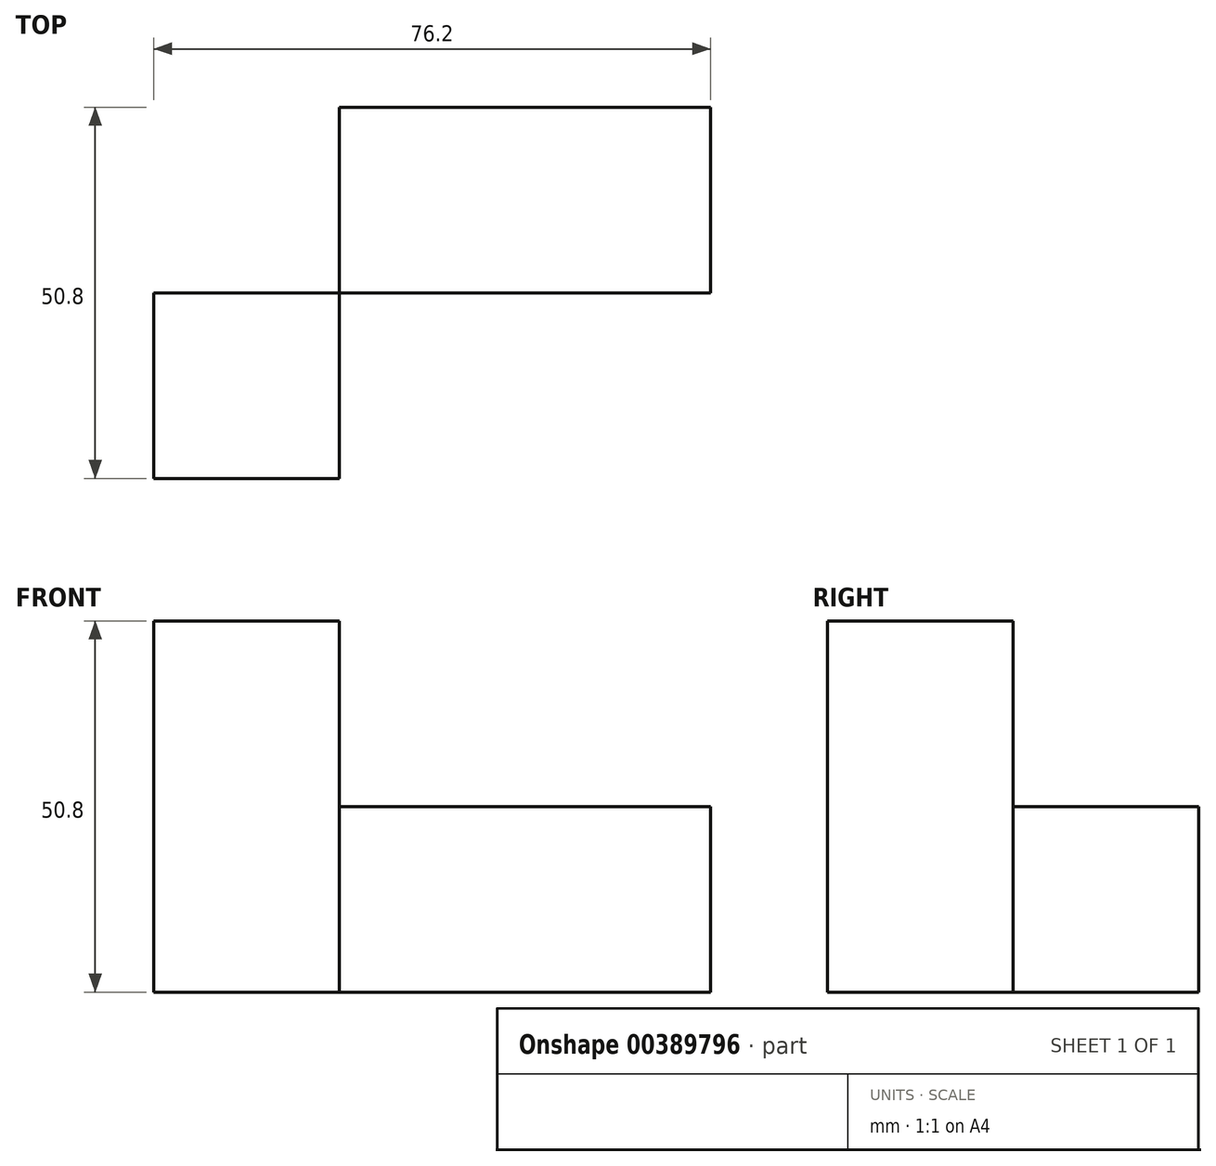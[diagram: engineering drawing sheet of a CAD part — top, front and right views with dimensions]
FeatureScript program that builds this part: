
annotation { "Feature Type Name" : "Feature", "Feature Type Description" : "" }
export const myFeature = defineFeature(function(context is Context, id is Id, definition is map)
    precondition{}
    {
        {
            var Q0;
            Q0=qCreatedBy(makeId("Top.planeOp"),FACE);
            var sketch = newSketch(context, id + "F0", { "sketchPlane" : qUnion([Q0])});
            skLineSegment(sketch, "E0.bottom", {"start": v(0, 0) * mm, "end": v(-25.4, 0) * mm});
            skLineSegment(sketch, "E0.top", {"start": v(0, 25.4) * mm, "end": v(-25.4, 25.4) * mm});
            skLineSegment(sketch, "E0.left", {"start": v(0, 0) * mm, "end": v(0, 25.4) * mm});
            skLineSegment(sketch, "E0.right", {"start": v(-25.4, 0) * mm, "end": v(-25.4, 25.4) * mm});
            skLineSegment(sketch, "E1.bottom", {"start": v(-25.4, 25.4) * mm, "end": v(0, 25.4) * mm});
            skLineSegment(sketch, "E1.top", {"start": v(-25.4, 50.8) * mm, "end": v(0, 50.8) * mm});
            skLineSegment(sketch, "E1.left", {"start": v(-25.4, 25.4) * mm, "end": v(-25.4, 50.8) * mm});
            skLineSegment(sketch, "E1.right", {"start": v(0, 25.4) * mm, "end": v(0, 50.8) * mm});
            skLineSegment(sketch, "E2.bottom", {"start": v(0, 50.8) * mm, "end": v(25.4, 50.8) * mm});
            skLineSegment(sketch, "E2.top", {"start": v(0, 25.4) * mm, "end": v(25.4, 25.4) * mm});
            skLineSegment(sketch, "E2.left", {"start": v(0, 50.8) * mm, "end": v(0, 25.4) * mm});
            skLineSegment(sketch, "E2.right", {"start": v(25.4, 50.8) * mm, "end": v(25.4, 25.4) * mm});
            skLineSegment(sketch, "E3.bottom", {"start": v(25.4, 25.4) * mm, "end": v(50.8, 25.4) * mm});
            skLineSegment(sketch, "E3.top", {"start": v(25.4, 50.8) * mm, "end": v(50.8, 50.8) * mm});
            skLineSegment(sketch, "E3.left", {"start": v(25.4, 25.4) * mm, "end": v(25.4, 50.8) * mm});
            skLineSegment(sketch, "E3.right", {"start": v(50.8, 25.4) * mm, "end": v(50.8, 50.8) * mm});
            skLineSegment(sketch, "E4.bottom", {"start": v(25.4, 25.4) * mm, "end": v(0, 25.4) * mm});
            skLineSegment(sketch, "E4.top", {"start": v(25.4, 0) * mm, "end": v(0, 0) * mm});
            skLineSegment(sketch, "E4.left", {"start": v(25.4, 25.4) * mm, "end": v(25.4, 0) * mm});
            skLineSegment(sketch, "E4.right", {"start": v(0, 25.4) * mm, "end": v(0, 0) * mm});
            skSolve(sketch);
        }
        {
            var Q0;
            Q0=makeQuery(id+"F0.imprint","IMPRINT",FACE,{"disambiguationData":[TD([[makeQuery(id+"F0.imprint","IMPRINT",EDGE,{"derivedFrom":sQuery(id+"F0.wireOp",EDGE,"E1.bottom")}),1.0]])]});
            var Q1;
            Q1=makeQuery(id+"F0.imprint","IMPRINT",FACE,{"disambiguationData":[TD([[makeQuery(id+"F0.imprint","IMPRINT",EDGE,{"derivedFrom":sQuery(id+"F0.wireOp",EDGE,"E2.bottom")}),-1.0]])]});
            var Q2;
            Q2=makeQuery(id+"F0.imprint","IMPRINT",FACE,{"disambiguationData":[TD([[makeQuery(id+"F0.imprint","IMPRINT",EDGE,{"derivedFrom":sQuery(id+"F0.wireOp",EDGE,"E3.bottom")}),1.0]])]});
            var Q3;
            Q3=makeQuery(id+"F0.imprint","IMPRINT",FACE,{"disambiguationData":[TD([[makeQuery(id+"F0.imprint","IMPRINT",EDGE,{"derivedFrom":sQuery(id+"F0.wireOp",EDGE,"E4.bottom")}),1.0]])]});
            extrude(context, id + "F1", {"entities" : qUnion([Q0, Q1, Q2, Q3]), "depth" : 25.4 * mm});
        }
        {
            var Q0;
            Q0=makeQuery(id+"F0.imprint","IMPRINT",FACE,{"disambiguationData":[TD([[makeQuery(id+"F0.imprint","IMPRINT",EDGE,{"derivedFrom":sQuery(id+"F0.wireOp",EDGE,"E0.bottom")}),-1.0]])]});
            extrude(context, id + "F2", {"entities" : qUnion([Q0]), "operationType" : NewBodyOperationType.ADD, "depth" : 50.8 * mm});
        }
    });
